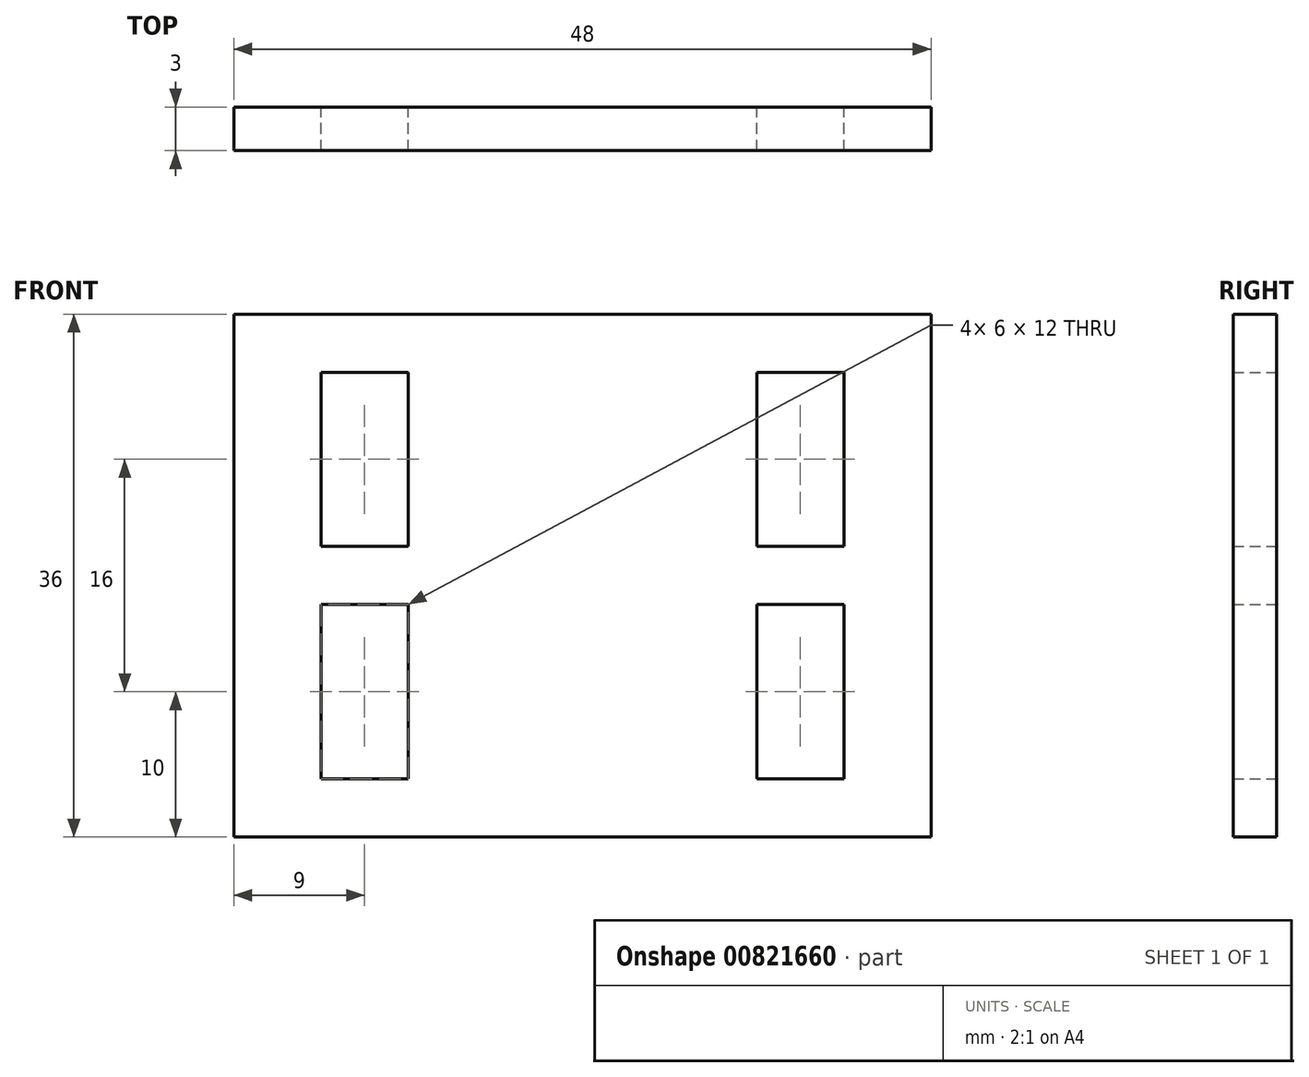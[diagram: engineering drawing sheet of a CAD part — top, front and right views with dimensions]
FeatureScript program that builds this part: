
annotation { "Feature Type Name" : "Feature", "Feature Type Description" : "" }
export const myFeature = defineFeature(function(context is Context, id is Id, definition is map)
    precondition{}
    {
        {
            var Q0;
            Q0=qCreatedBy(makeId("Front.planeOp"),FACE);
            var sketch = newSketch(context, id + "F0", { "sketchPlane" : qUnion([Q0])});
            skLineSegment(sketch, "E0.bottom", {"start": v(24, 18) * mm, "end": v(-24, 18) * mm});
            skLineSegment(sketch, "E0.top", {"start": v(24, -18) * mm, "end": v(-24, -18) * mm});
            skLineSegment(sketch, "E0.left", {"start": v(24, 18) * mm, "end": v(24, -18) * mm});
            skLineSegment(sketch, "E0.right", {"start": v(-24, 18) * mm, "end": v(-24, -18) * mm});
            skPoint(sketch, "E0.middle", {"position": v(0, 0) * mm});
            skLineSegment(sketch, "E1", {"start": v(-15, 18) * mm, "end": v(-15, -18) * mm, "construction": true});
            skLineSegment(sketch, "E2.0", {"start": v(-12, 14) * mm, "end": v(-12, 2) * mm});
            skLineSegment(sketch, "E3.0", {"start": v(-18, 14) * mm, "end": v(-18, 2) * mm});
            skLineSegment(sketch, "E4", {"start": v(-18, 14) * mm, "end": v(-12, 14) * mm});
            skLineSegment(sketch, "E5", {"start": v(-18, 2) * mm, "end": v(-12, 2) * mm});
            skLineSegment(sketch, "E6.MirrorCS", {"start": v(-12, -14) * mm, "end": v(-12, -2) * mm});
            skLineSegment(sketch, "E7.MirrorCS", {"start": v(-15, -18) * mm, "end": v(-15, 18) * mm, "construction": true});
            skLineSegment(sketch, "E8.MirrorCS", {"start": v(-18, -14) * mm, "end": v(-18, -2) * mm});
            skLineSegment(sketch, "E9.MirrorCS", {"start": v(-18, -14) * mm, "end": v(-12, -14) * mm});
            skLineSegment(sketch, "E10.MirrorCS", {"start": v(-18, -2) * mm, "end": v(-12, -2) * mm});
            skLineSegment(sketch, "E11.MirrorCS", {"start": v(18, 14) * mm, "end": v(18, 2) * mm});
            skLineSegment(sketch, "E12.MirrorCS", {"start": v(18, 14) * mm, "end": v(12, 14) * mm});
            skLineSegment(sketch, "E13.MirrorCS", {"start": v(12, 14) * mm, "end": v(12, 2) * mm});
            skLineSegment(sketch, "E14.MirrorCS", {"start": v(18, 2) * mm, "end": v(12, 2) * mm});
            skLineSegment(sketch, "E15.MirrorCS", {"start": v(12, -14) * mm, "end": v(12, -2) * mm});
            skLineSegment(sketch, "E16.MirrorCS", {"start": v(18, -14) * mm, "end": v(18, -2) * mm});
            skLineSegment(sketch, "E17.MirrorCS", {"start": v(18, -2) * mm, "end": v(12, -2) * mm});
            skLineSegment(sketch, "E18.MirrorCS", {"start": v(18, -14) * mm, "end": v(12, -14) * mm});
            skSolve(sketch);
        }
        {
            var Q0;
            Q0 = qSketchRegion(id + "F0", true);
            extrude(context, id + "F1", {"entities" : qUnion([Q0]), "depth" : 3 * mm, "offsetDistance" : 25 * mm});
        }
    });
